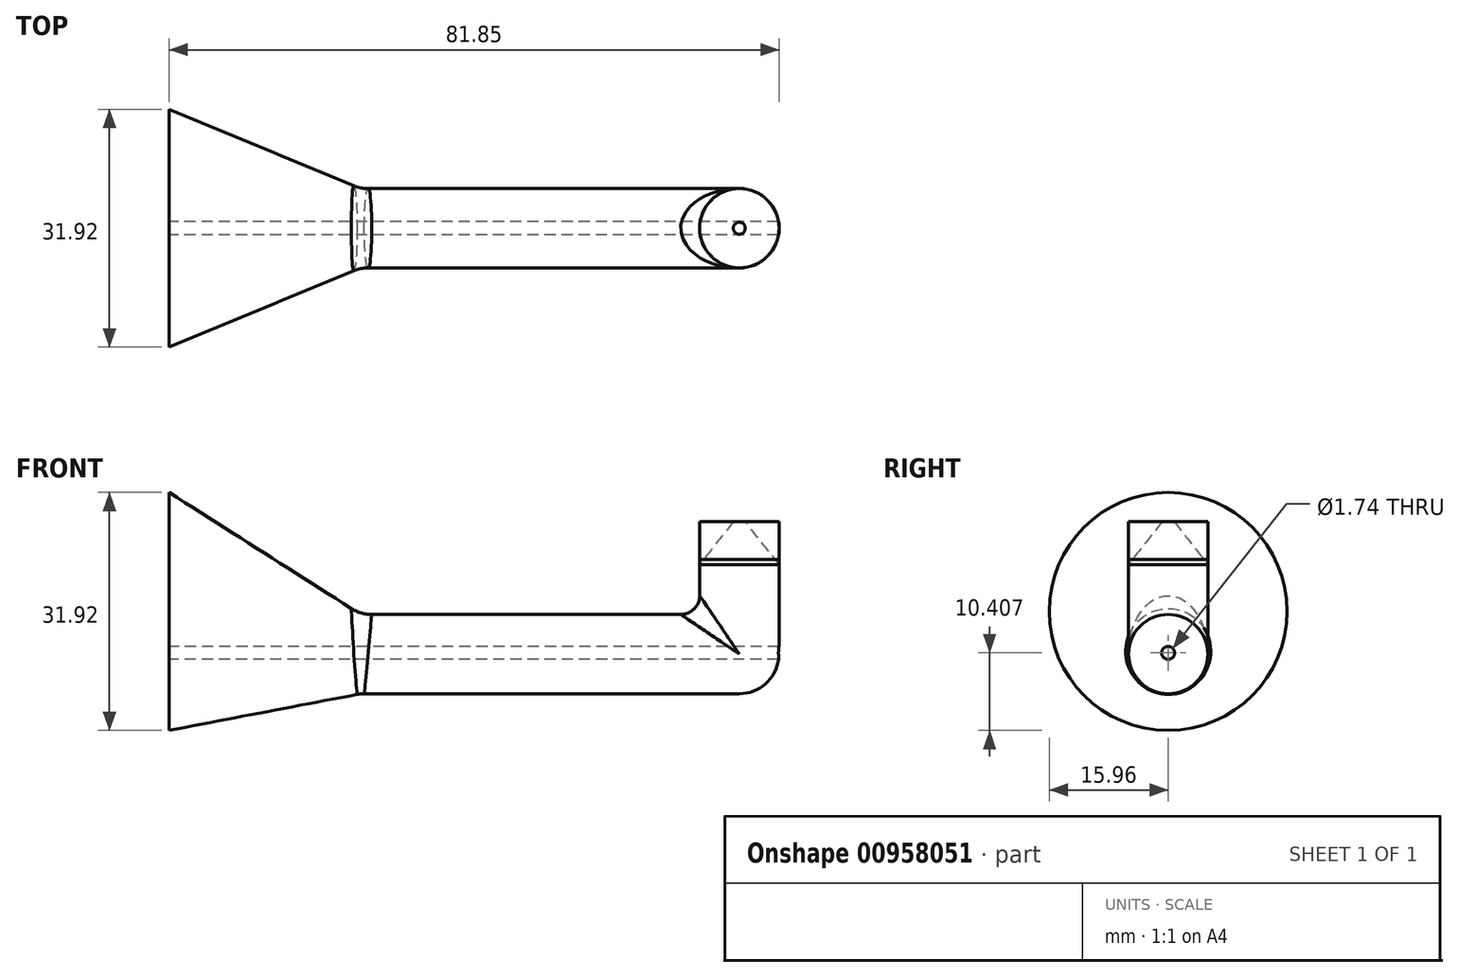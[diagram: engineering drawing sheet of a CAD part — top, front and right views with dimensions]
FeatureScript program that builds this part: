
annotation { "Feature Type Name" : "Feature", "Feature Type Description" : "" }
export const myFeature = defineFeature(function(context is Context, id is Id, definition is map)
    precondition{}
    {
        {
            var Q0;
            Q0=qCreatedBy(makeId("Front.planeOp"),FACE);
            var sketch = newSketch(context, id + "F0", { "sketchPlane" : qUnion([Q0])});
            skLineSegment(sketch, "E0", {"start": v(-62.73, 0) * mm, "end": v(-62.73, 12.4) * mm});
            skLineSegment(sketch, "E1", {"start": v(-62.73, 12.4) * mm, "end": v(-60.69, 12.4) * mm});
            skLineSegment(sketch, "E2", {"start": v(-60.69, 12.4) * mm, "end": v(-60.69, 15.96) * mm});
            skLineSegment(sketch, "E3", {"start": v(-60.69, 15.96) * mm, "end": v(-25.71, 15.96) * mm});
            skLineSegment(sketch, "E4", {"start": v(-25.71, 15.96) * mm, "end": v(-25.71, 0) * mm});
            skLineSegment(sketch, "E5", {"start": v(-75.8, 0) * mm, "end": v(0, 0) * mm, "construction": true});
            skSolve(sketch);
        }
        {
            var Q0;
            Q0=sQuery(id+"F0.wireOp",EDGE,"E3");
            var Q1;
            Q1=sQuery(id+"F0.wireOp",EDGE,"E2");
            var Q2;
            Q2=sQuery(id+"F0.wireOp",EDGE,"E1");
            var Q3;
            Q3=sQuery(id+"F0.wireOp",EDGE,"E0");
            var Q4;
            Q4=sQuery(id+"F0.wireOp",EDGE,"E4");
            var Q5;
            Q5=sQuery(id+"F0.wireOp",EDGE,"E5");
            revolve(context, id + "F1", {"bodyType" : ToolBodyType.SURFACE, "surfaceOperationType" : NewSurfaceOperationType.NEW, "surfaceEntities" : qUnion([Q0, Q1, Q2, Q3, Q4]), "axis" : qUnion([Q5]), "revolveType" : RevolveType.FULL});
        }
        {
            var Q0;
            Q0=qCreatedBy(makeId("Right.planeOp"),FACE);
            var sketch = newSketch(context, id + "F2", { "sketchPlane" : qUnion([Q0])});
            skCircle(sketch, "E6", {"center": v(0, -5.73) * mm, "radius": 5.32 * mm});
            skSolve(sketch);
        }
        {
            var Q0;
            Q0=makeQuery(id+"F1.opRevolve","SWEPT_FACE",FACE,{"disambiguationData":[OSD([sQuery(id+"F0.wireOp",EDGE,"E4")])]});
            var Q1;
            Q1=makeQuery(id+"F2.imprint","IMPRINT",FACE,{"disambiguationData":[TD([[makeQuery(id+"F2.imprint","IMPRINT",EDGE,{"derivedFrom":sQuery(id+"F2.wireOp",EDGE,"E6")}),1.0]])]});
            loft(context, id + "F3", {"sheetProfilesArray" : [{ "sheetProfileEntities" : qUnion([Q0]) }, { "sheetProfileEntities" : qUnion([Q1]) }]});
        }
        {
            var Q0;
            Q0=makeQuery(id+"F3.opLoft","CAP_FACE",FACE,{"disambiguationData":[OSD([makeQuery(id+"F2.imprint","IMPRINT",FACE,{"disambiguationData":[TD([[makeQuery(id+"F2.imprint","IMPRINT",EDGE,{"derivedFrom":sQuery(id+"F2.wireOp",EDGE,"E6")}),1.0]])]})])],"isStart":true});
            var sketch = newSketch(context, id + "F4", { "sketchPlane" : qUnion([Q0])});
            skSolve(sketch);
        }
        {
            var Q0;
            Q0 = qSketchRegion(id + "F4", true);
            var Q1;
            Q1=makeQuery(id+"F4.imprint","IMPRINT",FACE,{"disambiguationData":[TD([[makeQuery(id+"F4.imprint","IMPRINT",EDGE,{"derivedFrom":makeQuery(id+"F3.opLoft","MID_CAP_EDGE",EDGE,{"disambiguationData":[OSD([sQuery(id+"F2.wireOp",EDGE,"E6")])],"capPos":1.0})}),1.0]])]});
            extrude(context, id + "F5", {"entities" : qUnion([Q0, Q1]), "operationType" : NewBodyOperationType.ADD, "depth" : 50.8 * mm, "offsetDistance" : 25.4 * mm});
        }
        {
            var Q0;
            {var subQ0=sQuery(id+"F2.wireOp",EDGE,"E6");Q0=makeQuery(id+"F5.boolean.opBoolean","MERGE",EDGE,{"derivedFrom":[makeQuery(id+"F3.opLoft","MID_CAP_EDGE",EDGE,{"disambiguationData":[OSD([subQ0])],"capPos":1.0}),makeQuery(id+"F5.opExtrude","CAP_EDGE",EDGE,{"disambiguationData":[OSD([subQ0])],"isStart":true})]});}
            fillet(context, id + "F6", {"entities" : qUnion([Q0]), "radius" : 5.08 * mm, "tangentPropagation" : true, "allowEdgeOverflow" : false});
        }
        {
            var Q0;
            Q0=qCreatedBy(makeId("Top.planeOp"),FACE);
            var Q1;
            Q1=sQuery(id+"F2.wireOp",VERTEX,"E6.center");
            cPlane(context, id + "F7", {"entities" : qUnion([Q0, Q1]), "cplaneType" : CPlaneType.PLANE_POINT, "offset" : 25.4 * mm, "width" : 152.4 * mm, "height" : 152.4 * mm});
        }
        {
            var Q0;
            Q0=qCreatedBy(id+"F7.planeOp",FACE);
            var sketch = newSketch(context, id + "F8", { "sketchPlane" : qUnion([Q0])});
            skLineSegment(sketch, "E7", {"start": v(50.8, -5.32) * mm, "end": v(1, -5.32) * mm});
            skLineSegment(sketch, "E8", {"start": v(1, 5.32) * mm, "end": v(50.8, 5.32) * mm});
            skCircle(sketch, "E9", {"center": v(50.8, 0) * mm, "radius": 5.32 * mm});
            skSolve(sketch);
        }
        {
            var Q0;
            Q0 = qSketchRegion(id + "F8", true);
            extrude(context, id + "F9", {"entities" : qUnion([Q0]), "operationType" : NewBodyOperationType.ADD, "depth" : 17.78 * mm, "offsetDistance" : 25.4 * mm});
        }
        {
            var Q0;
            Q0=makeQuery(id+"F9.opExtrude","CAP_FACE",FACE,{"disambiguationData":[OSD([sQuery(id+"F8.wireOp",EDGE,"E9")])],"isStart":true});
            var Q1;
            Q1=makeQuery(id+"F9.boolean.opBoolean","INTERSECT",EDGE,{"derivedFrom":[makeQuery(id+"F5.opExtrude","CAP_FACE",FACE,{"disambiguationData":[OSD([sQuery(id+"F2.wireOp",EDGE,"E6")])],"isStart":false}),makeQuery(id+"F9.opExtrude","CAP_FACE",FACE,{"disambiguationData":[OSD([sQuery(id+"F8.wireOp",EDGE,"E9")])],"isStart":true})]});
            revolve(context, id + "F10", {"operationType" : NewBodyOperationType.ADD, "surfaceOperationType" : NewSurfaceOperationType.NEW, "entities" : qUnion([Q0]), "axis" : qUnion([Q1]), "revolveType" : RevolveType.ONE_DIRECTION, "oppositeDirection" : true, "angle" : 90 * degree});
        }
        {
            var Q0;
            Q0=makeQuery(id+"F9.boolean.opBoolean","INTERSECT",EDGE,{"derivedFrom":[makeQuery(id+"F5.opExtrude","SWEPT_FACE",FACE,{"disambiguationData":[OSD([sQuery(id+"F2.wireOp",EDGE,"E6")])]}),makeQuery(id+"F9.opExtrude","SWEPT_FACE",FACE,{"disambiguationData":[OSD([sQuery(id+"F8.wireOp",EDGE,"E9")])]})]});
            fillet(context, id + "F11", {"entities" : qUnion([Q0]), "radius" : 2.54 * mm, "tangentPropagation" : true, "allowEdgeOverflow" : false});
        }
        {
            var Q0;
            Q0=makeQuery(id+"F9.opExtrude","CAP_FACE",FACE,{"disambiguationData":[OSD([sQuery(id+"F8.wireOp",EDGE,"E9")])],"isStart":false});
            var sketch = newSketch(context, id + "F12", { "sketchPlane" : qUnion([Q0])});
            skCircle(sketch, "E10", {"center": v(50.8, 0) * mm, "radius": 0.8 * mm});
            skSolve(sketch);
        }
        {
            var Q0;
            Q0=qCreatedBy(makeId("Front.planeOp"),FACE);
            var sketch = newSketch(context, id + "F13", { "sketchPlane" : qUnion([Q0])});
            skLineSegment(sketch, "E11", {"start": v(50.8, 12.05) * mm, "end": v(50.8, -12.5) * mm, "construction": true});
            skPoint(sketch, "E12", {"position": v(50.8, 6.27) * mm});
            skSolve(sketch);
        }
        {
            var Q0;
            Q0=qCreatedBy(makeId("Top.planeOp"),FACE);
            var Q1;
            Q1=sQuery(id+"F13.wireOp",VERTEX,"E12");
            cPlane(context, id + "F14", {"entities" : qUnion([Q0, Q1]), "cplaneType" : CPlaneType.PLANE_POINT, "offset" : 25.4 * mm, "width" : 152.4 * mm, "height" : 152.4 * mm});
        }
        {
            var Q0;
            Q0=qCreatedBy(id+"F14.planeOp",FACE);
            var sketch = newSketch(context, id + "F15", { "sketchPlane" : qUnion([Q0])});
            skCircle(sketch, "E13", {"center": v(50.8, 0) * mm, "radius": 5.34 * mm});
            skSolve(sketch);
        }
        {
            var Q0;
            Q0=makeQuery(id+"F1.opRevolve","SWEPT_FACE",FACE,{"disambiguationData":[OSD([sQuery(id+"F0.wireOp",EDGE,"E0")])]});
            var sketch = newSketch(context, id + "F16", { "sketchPlane" : qUnion([Q0])});
            skCircle(sketch, "E14", {"center": v(0, -9.33) * mm, "radius": 0.97 * mm});
            skCircle(sketch, "E15", {"center": v(0, -5.55) * mm, "radius": 0.87 * mm});
            skSolve(sketch);
        }
        {
            var Q0;
            Q0=makeQuery(id+"F16.imprint","IMPRINT",FACE,{"disambiguationData":[TD([[makeQuery(id+"F16.imprint","IMPRINT",EDGE,{"derivedFrom":sQuery(id+"F16.wireOp",EDGE,"E15")}),1.0]])]});
            extrude(context, id + "F17", {"entities" : qUnion([Q0]), "operationType" : NewBodyOperationType.REMOVE, "endBound" : BoundingType.THROUGH_ALL, "depth" : 25.4 * mm, "offsetDistance" : 25.4 * mm});
        }
        {
            var Q0;
            Q0=makeQuery(id+"F15.imprint","IMPRINT",FACE,{"disambiguationData":[TD([[makeQuery(id+"F15.imprint","IMPRINT",EDGE,{"derivedFrom":sQuery(id+"F15.wireOp",EDGE,"E13")}),1.0]])]});
            var Q1;
            Q1=makeQuery(id+"F12.imprint","IMPRINT",FACE,{"disambiguationData":[TD([[makeQuery(id+"F12.imprint","IMPRINT",EDGE,{"derivedFrom":sQuery(id+"F12.wireOp",EDGE,"E10")}),1.0]])]});
            loft(context, id + "F18", {"sheetProfilesArray" : [{ "sheetProfileEntities" : qUnion([Q0]) }, { "sheetProfileEntities" : qUnion([Q1]) }]});
        }
        {
            var Q0;
            Q0=makeQuery(id+"F18.opLoft","MID_CAP_EDGE",EDGE,{"disambiguationData":[OSD([sQuery(id+"F15.wireOp",EDGE,"E13")])],"capPos":0.0});
            var Q1;
            Q1=makeQuery(id+"F18.opLoft","MID_CAP_EDGE",EDGE,{"disambiguationData":[OSD([sQuery(id+"F12.wireOp",EDGE,"E10")])],"capPos":1.0});
            loft(context, id + "F19", {"bodyType" : ToolBodyType.SURFACE, "wireProfilesArray" : [{ "wireProfileEntities" : qUnion([Q0]) }, { "wireProfileEntities" : qUnion([Q1]) }]});
        }
        {
            var Q0;
            Q0=makeQuery(id+"F9.opExtrude","CAP_FACE",FACE,{"disambiguationData":[OSD([sQuery(id+"F8.wireOp",EDGE,"E9")])],"isStart":false});
            extrude(context, id + "F20", {"entities" : qUnion([Q0]), "oppositeDirection" : true, "depth" : 5.08 * mm, "offsetDistance" : 25.4 * mm});
        }
        {
            var Q0;
            Q0=makeQuery(id+"F1.opRevolve","SWEPT_BODY",BODY,{"disambiguationData":[OSD([sQuery(id+"F0.wireOp",EDGE,"E0")])]});
            var Q1;
            Q1=makeQuery(id+"F19.opLoft","SWEPT_BODY",BODY,{"disambiguationData":[OSD([sQuery(id+"F12.wireOp",EDGE,"E10"),sQuery(id+"F15.wireOp",EDGE,"E13")])]});
            deleteBodies(context, id + "F21", {"entities" : qUnion([Q0, Q1])});
        }
    });
